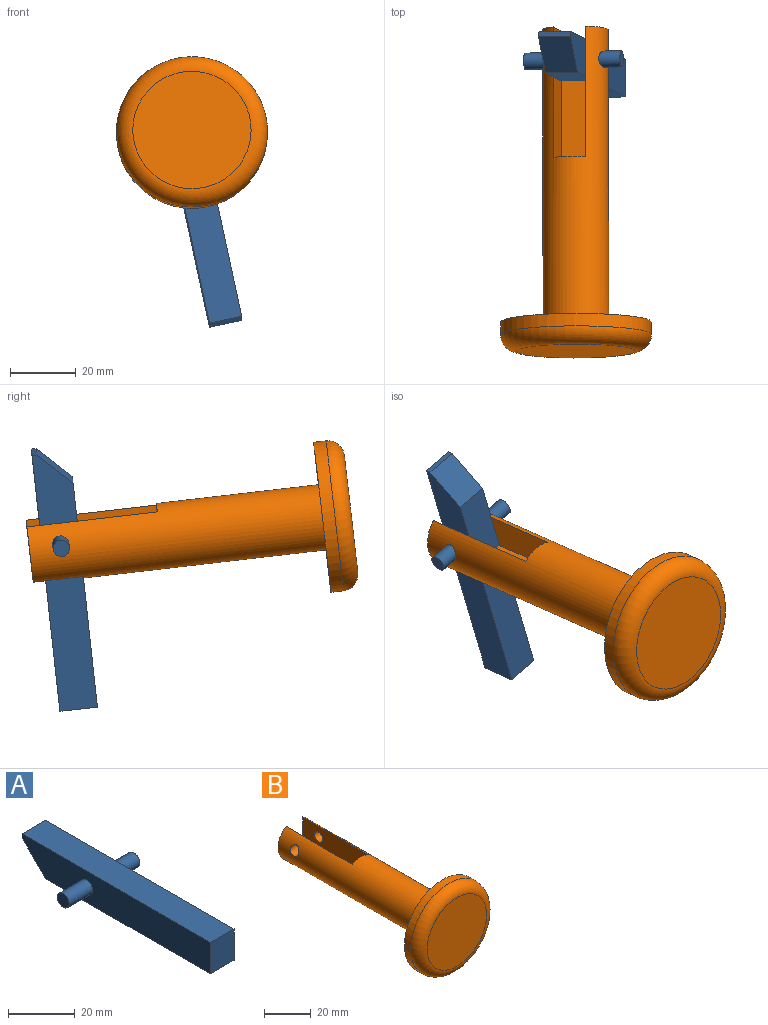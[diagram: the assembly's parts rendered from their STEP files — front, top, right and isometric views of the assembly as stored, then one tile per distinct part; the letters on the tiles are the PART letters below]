
ASSEMBLY  parts=2 mates=1
PART A: 11 faces, bbox 30x80x11.5 mm
  f0: plane 11.48x10mm, normal (0,-1,0), area 114.8mm2, adj f1,f3,f4,f5
  f1: plane 80x11.48mm, normal (1,0,0), area 848.8mm2, adj f0,f2,f4,f5,f8,f10
  f2: plane 10x1.48mm, normal (0,1,0), area 14.8mm2, adj f1,f3,f4,f10
  f3: plane 80x11.48mm, normal (-1,0,0), area 848.8mm2, adj f0,f2,f4,f5,f7,f10
  f4: plane 80x10mm, normal (0,0,1), area 800mm2, adj f0,f1,f2,f3
  f5: plane 70x10mm, normal (0,0,-1), area 700mm2, adj f0,f1,f3,f10
  f6: plane 5x5mm, normal (-1,0,0), area 19.6mm2, adj f7
  f7: cylinder r=2.5mm len=10mm, axis (-1,0,0), area 157.1mm2, adj f3,f6
  f8: cylinder r=2.5mm len=10mm, axis (-1,0,0), area 157.1mm2, adj f1,f9
  f9: plane 5x5mm, normal (1,0,0), area 19.6mm2, adj f8
  f10: plane 10x10mm, normal (0,0.71,-0.71), area 141.4mm2, adj f1,f2,f3,f5
PART B: 14 faces, bbox 49.8x98.5x49.8 mm
  f0: cylinder r=10mm len=89.7mm, axis (0,-1,0), area 5018.8mm2, adj f1,f2,f3,f7,f9,f10,f11,f12
  f1: plane 17.32x5mm, normal (0,1,0), area 61.4mm2, adj f0,f9
  f2: plane 17.32x5mm, normal (0,1,0), area 61.4mm2, adj f0,f7
  f3: plane 46x46mm, normal (0,1,0), area 1347.7mm2, adj f0,f4
  f4: cylinder r=23mm len=46mm, axis (0,-1,0), area 552.9mm2, adj f3,f5
  f5: torus R=18mm, axis (0,-1,0), area 1045.3mm2, adj f4,f6
  f6: plane 36x36mm, normal (0,-1,0), area 1017.9mm2, adj f5
  f7: plane 40x17.32mm, normal (-1,0,0), area 527.2mm2, adj f0,f2,f8,f10,f11,f13
  f8: plane 25x10mm, normal (0,0,1), area 250mm2, adj f7,f9,f10,f11
  f9: plane 40x17.32mm, normal (1,0,0), area 527.2mm2, adj f0,f1,f8,f10,f11,f12
  f10: plane 12.82x10mm, normal (0,1,0), area 123.9mm2, adj f0,f7,f8,f9
  f11: plane 10x7.18mm, normal (0,1,0), area 67.4mm2, adj f0,f7,f8,f9
  f12: cylinder r=2.5mm len=5mm, axis (1,0,0), area 68.8mm2, adj f0,f9
  f13: cylinder r=2.5mm len=5mm, axis (1,0,0), area 68.8mm2, adj f0,f7
PLACE A rot(axis=(-0.08,0.74,0.67),172.1deg) t=(33.91,98.21,-57.03)mm
PLACE B rot(axis=(-0.48,-0.88,0.06),13.8deg) t=(28.51,29.75,0.79)mm
MATE revolute A.f7 <-> B.f12  axis (0.98,0.03,0.21) through (42.43,109.99,-2.46)mm
